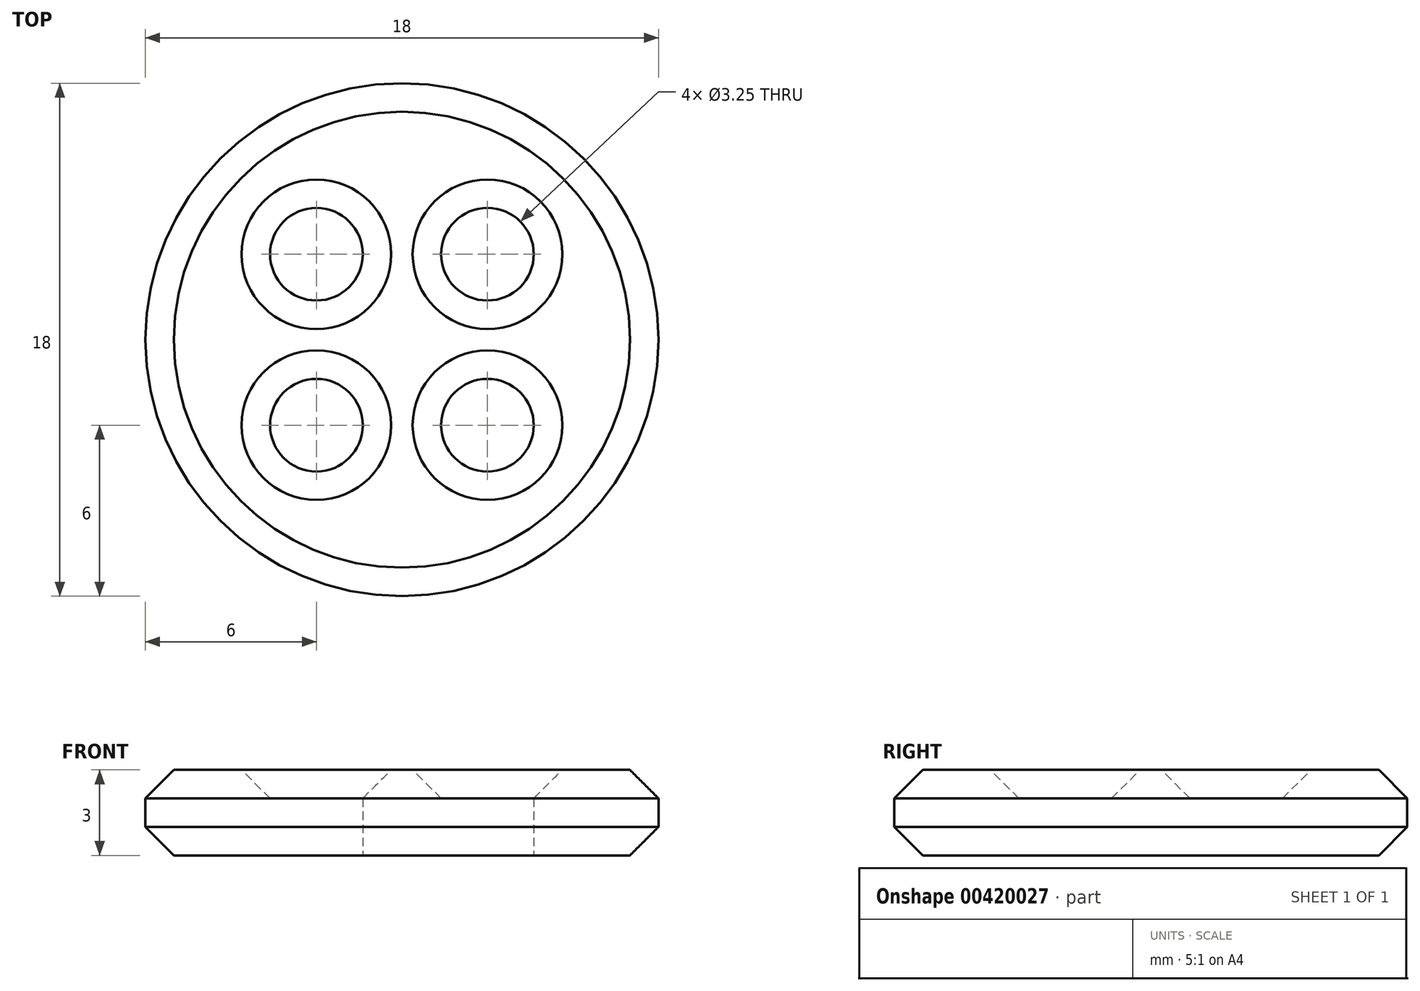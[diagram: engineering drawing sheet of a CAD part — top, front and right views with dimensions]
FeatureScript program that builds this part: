
annotation { "Feature Type Name" : "Feature", "Feature Type Description" : "" }
export const myFeature = defineFeature(function(context is Context, id is Id, definition is map)
    precondition{}
    {
        {
            var Q0;
            Q0=qCreatedBy(makeId("Top.planeOp"),FACE);
            var sketch = newSketch(context, id + "F0", { "sketchPlane" : qUnion([Q0])});
            skCircle(sketch, "E0", {"center": v(0, 0) * mm, "radius": 9 * mm});
            skCircle(sketch, "E1", {"center": v(3, 3) * mm, "radius": 1.63 * mm});
            skCircle(sketch, "E2.1.0", {"center": v(-3, 3) * mm, "radius": 1.63 * mm});
            skCircle(sketch, "E2.2.0", {"center": v(-3, -3) * mm, "radius": 1.63 * mm});
            skCircle(sketch, "E2.3.0", {"center": v(3, -3) * mm, "radius": 1.63 * mm});
            skSolve(sketch);
        }
        {
            var Q0;
            Q0=makeQuery(id+"F0.imprint","IMPRINT",FACE,{"disambiguationData":[TD([[makeQuery(id+"F0.imprint","IMPRINT",EDGE,{"derivedFrom":sQuery(id+"F0.wireOp",EDGE,"E0")}),1.0]])]});
            extrude(context, id + "F1", {"entities" : qUnion([Q0]), "depth" : 3 * mm});
        }
        {
            var Q0;
            Q0=makeQuery(id+"F1.opExtrude","CAP_FACE",FACE,{"disambiguationData":[OSD([sQuery(id+"F0.wireOp",EDGE,"E0"),sQuery(id+"F0.wireOp",EDGE,"E1"),sQuery(id+"F0.wireOp",EDGE,"E2.1.0"),sQuery(id+"F0.wireOp",EDGE,"E2.2.0"),sQuery(id+"F0.wireOp",EDGE,"E2.3.0")])],"isStart":false});
            var Q1;
            Q1=makeQuery(id+"F1.opExtrude","CAP_EDGE",EDGE,{"disambiguationData":[OSD([sQuery(id+"F0.wireOp",EDGE,"E0")])],"isStart":true});
            chamfer(context, id + "F2", {"entities" : qUnion([Q0, Q1]), "width" : 1 * mm, "tangentPropagation" : true});
        }
    });
